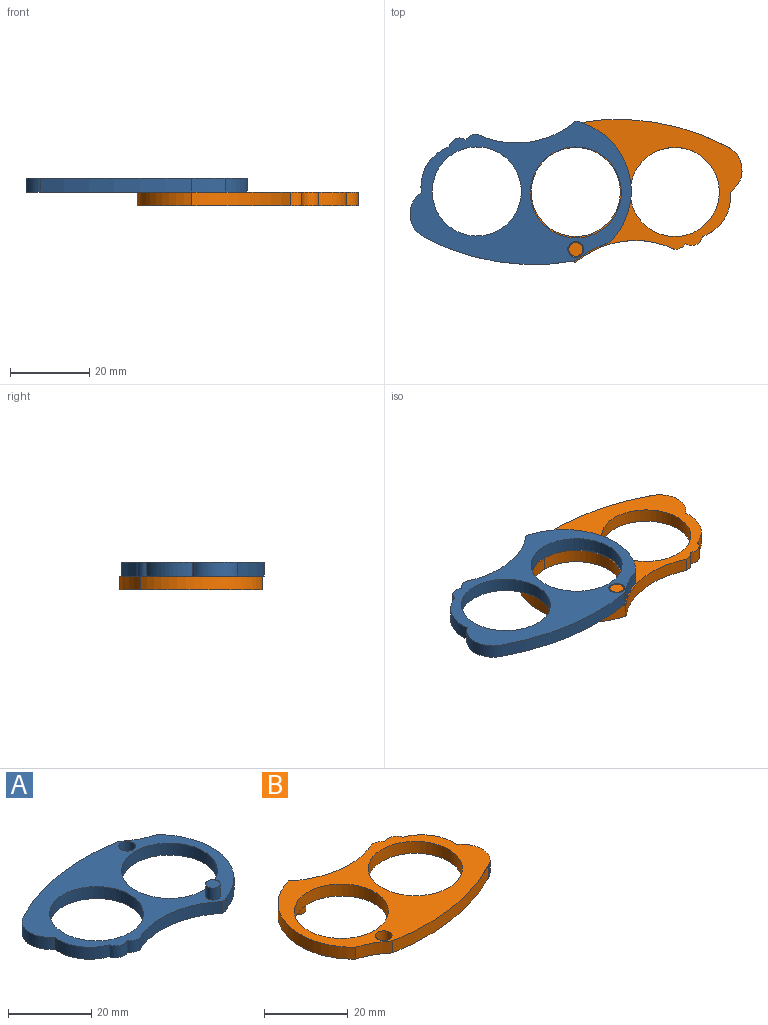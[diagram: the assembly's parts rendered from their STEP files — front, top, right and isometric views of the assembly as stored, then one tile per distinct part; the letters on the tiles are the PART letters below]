
ASSEMBLY  parts=2 mates=1
PART A: 16 faces, bbox 55.9x36.2x7 mm
  f0: cylinder r=6.61mm len=11.36mm, axis (0,0,-1), area 48mm2, adj f1,f10,f12,f13
  f1: cylinder r=10.61mm len=11.5mm, axis (0,0,-1), area 51mm2, adj f0,f2,f12,f13
  f2: cylinder r=2.79mm len=4.29mm, axis (0,0,-1), area 19.2mm2, adj f1,f3,f12,f13
  f3: cylinder r=3.25mm len=3.5mm, axis (0,0,-1), area 11.2mm2, adj f2,f4,f12,f13
  f4: cylinder r=23.27mm len=25mm, axis (0,0,-1), area 93.2mm2, adj f3,f5,f12,f13
  f5: cylinder r=3.25mm len=3.5mm, axis (0,0,-1), area 6.3mm2, adj f4,f6,f12,f13
  f6: cylinder r=18.09mm len=30.23mm, axis (0,0,-1), area 130.1mm2, adj f5,f7,f12,f13
  f7: cylinder r=23.27mm len=8.42mm, axis (0,0,-1), area 33.7mm2, adj f6,f10,f12,f13
  f8: cylinder r=11.5mm len=23mm, axis (0,0,-1), area 252.9mm2, adj f12,f13
  f9: cylinder r=11.25mm len=22.5mm, axis (0,0,-1), area 247.4mm2, adj f12,f13
  f10: cylinder r=59.02mm len=38.22mm, axis (0,0,-1), area 137.9mm2, adj f0,f7,f12,f13
  f11: cylinder r=2mm len=4mm, axis (0,0,-1), area 44mm2, adj f12,f13
  f12: plane 55.88x36.22mm, normal (0,0,1), area 691.8mm2, adj f0,f1,f2,f3,f4,f5,f6,f7
  f13: plane 55.88x36.22mm, normal (0,0,-1), area 701.5mm2, adj f0,f1,f2,f3,f4,f5,f6,f7
  f14: cylinder r=1.75mm len=3.5mm, axis (0,0,-1), area 38.5mm2, adj f12,f15
  f15: plane 3.5x3.5mm, normal (0,0,1), area 9.6mm2, adj f14
PART B: 19 faces, bbox 55.7x36.1x7 mm
  f0: cylinder r=23.27mm len=25mm, axis (0,0,-1), area 93.2mm2, adj f1,f12,f15,f16
  f1: cylinder r=18.09mm len=30.67mm, axis (0,0,-1), area 135.5mm2, adj f0,f2,f15,f16
  f2: cylinder r=23.27mm len=8.13mm, axis (0,0,-1), area 32.7mm2, adj f1,f3,f15,f16
  f3: cylinder r=59.02mm len=38.24mm, axis (0,0,-1), area 138mm2, adj f2,f4,f15,f16
  f4: cylinder r=6.61mm len=3.5mm, axis (0,0,-1), area 0.9mm2, adj f3,f5,f15,f16
  f5: cylinder r=41.76mm len=3.5mm, axis (0,0,-1), area 2.9mm2, adj f4,f6,f15,f16
  f6: cylinder r=6.61mm len=11.21mm, axis (0,0,-1), area 46.9mm2, adj f5,f7,f15,f16
  f7: cylinder r=10.58mm len=11.25mm, axis (0,0,-1), area 50.1mm2, adj f6,f8,f15,f16
  f8: cylinder r=2.79mm len=4.29mm, axis (0,0,-1), area 19.2mm2, adj f7,f12,f15,f16
  f9: cylinder r=11.25mm len=22.5mm, axis (0,0,-1), area 247.1mm2, adj f10,f13,f15,f16
  f10: cylinder r=41.76mm len=3.5mm, axis (0,0,-1), area 0mm2, adj f9,f13,f15,f16
  f11: cylinder r=11.25mm len=22.5mm, axis (0,0,-1), area 247.4mm2, adj f15,f16
  f12: cylinder r=3.25mm len=3.5mm, axis (0,0,-1), area 11.2mm2, adj f0,f8,f15,f16
  f13: cylinder r=3.06mm len=3.5mm, axis (0,0,-1), area 0.3mm2, adj f9,f10,f15,f16
  f14: cylinder r=2mm len=4mm, axis (0,0,-1), area 44mm2, adj f15,f16
  f15: plane 55.74x36.09mm, normal (0,0,1), area 707mm2, adj f0,f1,f2,f3,f4,f5,f6,f7
  f16: plane 55.74x36.09mm, normal (0,0,-1), area 697.4mm2, adj f0,f1,f2,f3,f4,f5,f6,f7
  f17: plane 3.5x3.5mm, normal (0,0,-1), area 9.6mm2, adj f18
  f18: cylinder r=1.75mm len=3.5mm, axis (0,0,-1), area 38.5mm2, adj f16,f17
PLACE A rot(axis=(-1,0,0),180deg) t=(68.86,-3.61,-19.44)mm
PLACE B rot(axis=(-1,0,0),180deg) t=(-31.24,-5.76,-22.94)mm
MATE revolute A.f11 <-> B.f18  axis (0,0,1) through (68.86,-17.99,-19.44)mm
